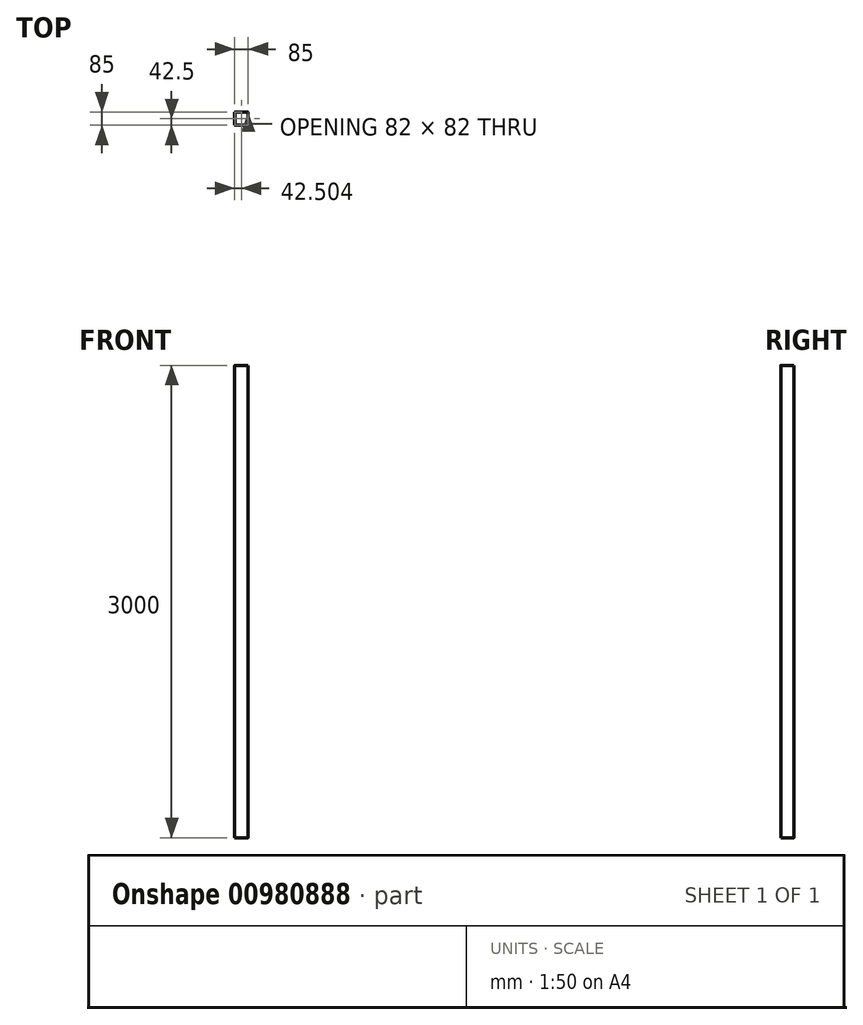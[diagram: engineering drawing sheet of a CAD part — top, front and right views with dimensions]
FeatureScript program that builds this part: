
annotation { "Feature Type Name" : "Feature", "Feature Type Description" : "" }
export const myFeature = defineFeature(function(context is Context, id is Id, definition is map)
    precondition{}
    {
        {
            var Q0;
            Q0=qCreatedBy(makeId("Top.planeOp"),FACE);
            var sketch = newSketch(context, id + "F0", { "sketchPlane" : qUnion([Q0])});
            skLineSegment(sketch, "E0.bottom", {"start": v(-96.1, 83.86) * mm, "end": v(-17.1, 83.86) * mm});
            skLineSegment(sketch, "E0.top", {"start": v(-96.1, -1.14) * mm, "end": v(-17.1, -1.14) * mm});
            skLineSegment(sketch, "E0.left", {"start": v(-99.1, 80.86) * mm, "end": v(-99.1, 1.86) * mm});
            skLineSegment(sketch, "E0.right", {"start": v(-14.1, 80.86) * mm, "end": v(-14.1, 1.86) * mm});
            skLineSegment(sketch, "E1.0", {"start": v(-96.6, 0.36) * mm, "end": v(-16.6, 0.36) * mm});
            skLineSegment(sketch, "E1.1", {"start": v(-97.6, 81.36) * mm, "end": v(-97.6, 1.36) * mm});
            skLineSegment(sketch, "E1.2", {"start": v(-96.6, 82.36) * mm, "end": v(-15.6, 82.36) * mm});
            skLineSegment(sketch, "E1.3", {"start": v(-15.6, 82.36) * mm, "end": v(-15.6, 1.36) * mm});
            skPoint(sketch, "E2.visualSharp", {"position": v(-99.1, -1.14) * mm});
            skArc(sketch, "E2.filletArc", {"start": v(-99.1, 1.86) * mm, "mid": v(-98.23, -0.26) * mm, "end": v(-96.1, -1.14) * mm});
            skPoint(sketch, "E3.visualSharp", {"position": v(-99.1, 83.86) * mm});
            skArc(sketch, "E3.filletArc", {"start": v(-96.1, 83.86) * mm, "mid": v(-98.23, 82.98) * mm, "end": v(-99.1, 80.86) * mm});
            skPoint(sketch, "E4.visualSharp", {"position": v(-14.1, 83.86) * mm});
            skArc(sketch, "E4.filletArc", {"start": v(-14.1, 80.86) * mm, "mid": v(-14.98, 82.98) * mm, "end": v(-17.1, 83.86) * mm});
            skPoint(sketch, "E5.visualSharp", {"position": v(-14.1, -1.14) * mm});
            skArc(sketch, "E5.filletArc", {"start": v(-17.1, -1.14) * mm, "mid": v(-14.98, -0.26) * mm, "end": v(-14.1, 1.86) * mm});
            skPoint(sketch, "E6.visualSharp", {"position": v(-15.6, 0.36) * mm});
            skArc(sketch, "E6.filletArc", {"start": v(-16.6, 0.36) * mm, "mid": v(-15.9, 0.65) * mm, "end": v(-15.6, 1.36) * mm});
            skPoint(sketch, "E7.visualSharp", {"position": v(-97.6, 0.36) * mm});
            skArc(sketch, "E7.filletArc", {"start": v(-97.6, 1.36) * mm, "mid": v(-97.31, 0.65) * mm, "end": v(-96.6, 0.36) * mm});
            skPoint(sketch, "E8.visualSharp", {"position": v(-97.6, 82.36) * mm});
            skArc(sketch, "E8.filletArc", {"start": v(-96.6, 82.36) * mm, "mid": v(-97.31, 82.07) * mm, "end": v(-97.6, 81.36) * mm});
            skSolve(sketch);
        }
        {
            var Q0;
            Q0=makeQuery(id+"F0.imprint","IMPRINT",FACE,{"disambiguationData":[TD([[makeQuery(id+"F0.imprint","IMPRINT",EDGE,{"derivedFrom":sQuery(id+"F0.wireOp",EDGE,"E0.bottom")}),-1.0]])]});
            extrude(context, id + "F1", {"entities" : qUnion([Q0]), "depth" : 3000 * mm, "offsetDistance" : 25 * mm});
        }
    });
